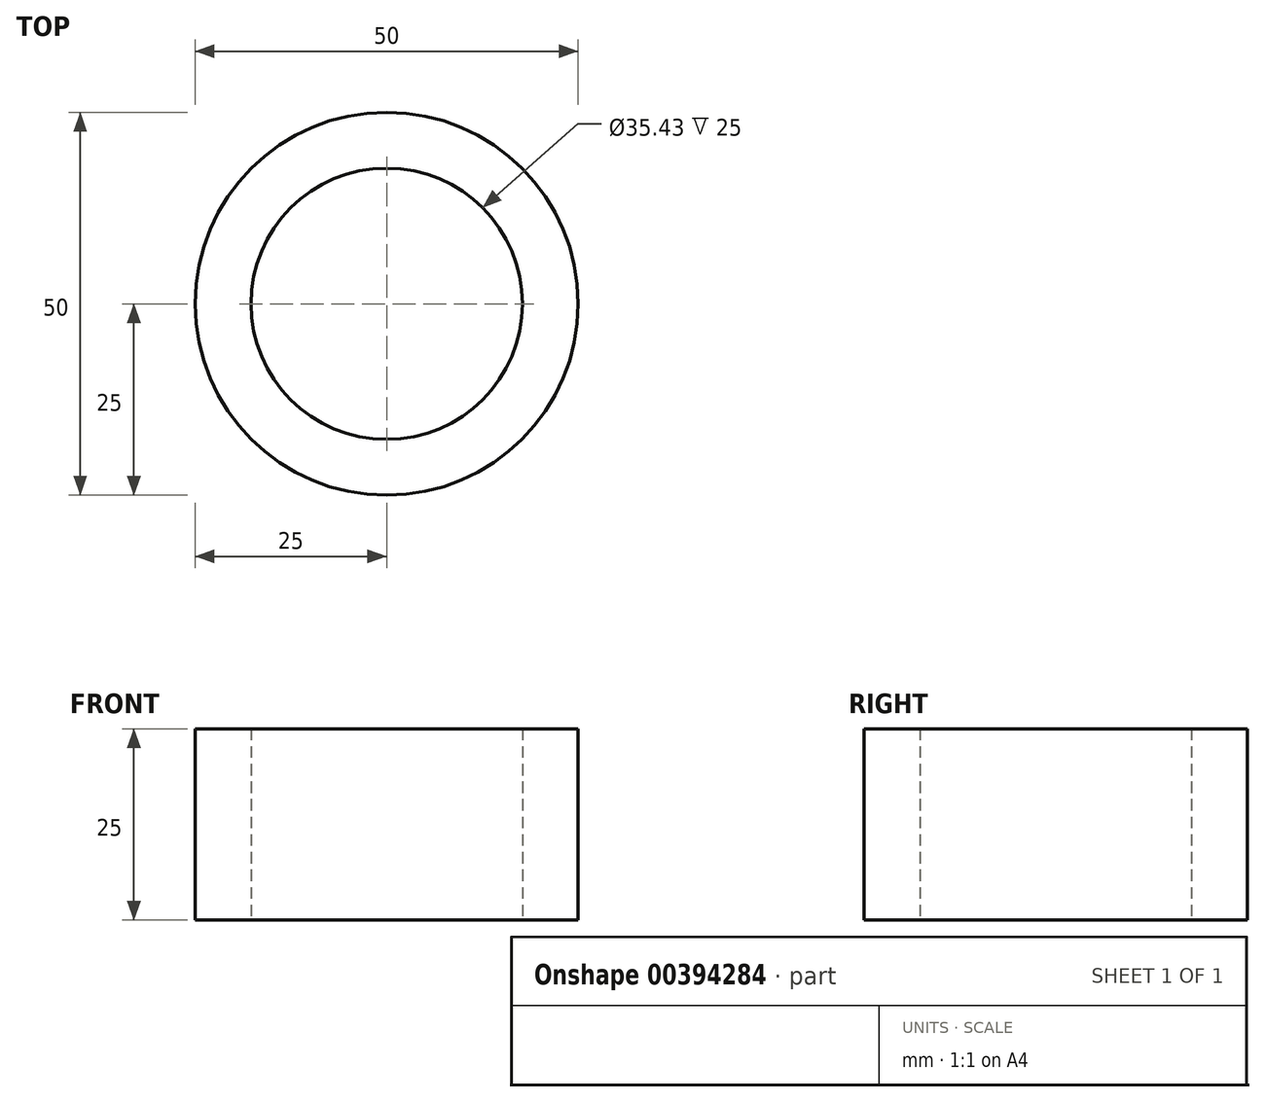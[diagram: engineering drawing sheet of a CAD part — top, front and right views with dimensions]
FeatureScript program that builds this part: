
annotation { "Feature Type Name" : "Feature", "Feature Type Description" : "" }
export const myFeature = defineFeature(function(context is Context, id is Id, definition is map)
    precondition{}
    {
        {
            var Q0;
            Q0=qCreatedBy(makeId("Top.planeOp"),FACE);
            var sketch = newSketch(context, id + "F0", { "sketchPlane" : qUnion([Q0])});
            skCircle(sketch, "E0", {"center": v(0, 0) * mm, "radius": 17.71 * mm});
            skCircle(sketch, "E1", {"center": v(0, 0) * mm, "radius": 25 * mm});
            skSolve(sketch);
        }
        {
            var Q0;
            Q0=makeQuery(id+"F0.imprint","IMPRINT",FACE,{"disambiguationData":[TD([[makeQuery(id+"F0.imprint","IMPRINT",EDGE,{"derivedFrom":sQuery(id+"F0.wireOp",EDGE,"E0")}),-1.0]])]});
            extrude(context, id + "F1", {"entities" : qUnion([Q0]), "depth" : 25 * mm});
        }
    });
